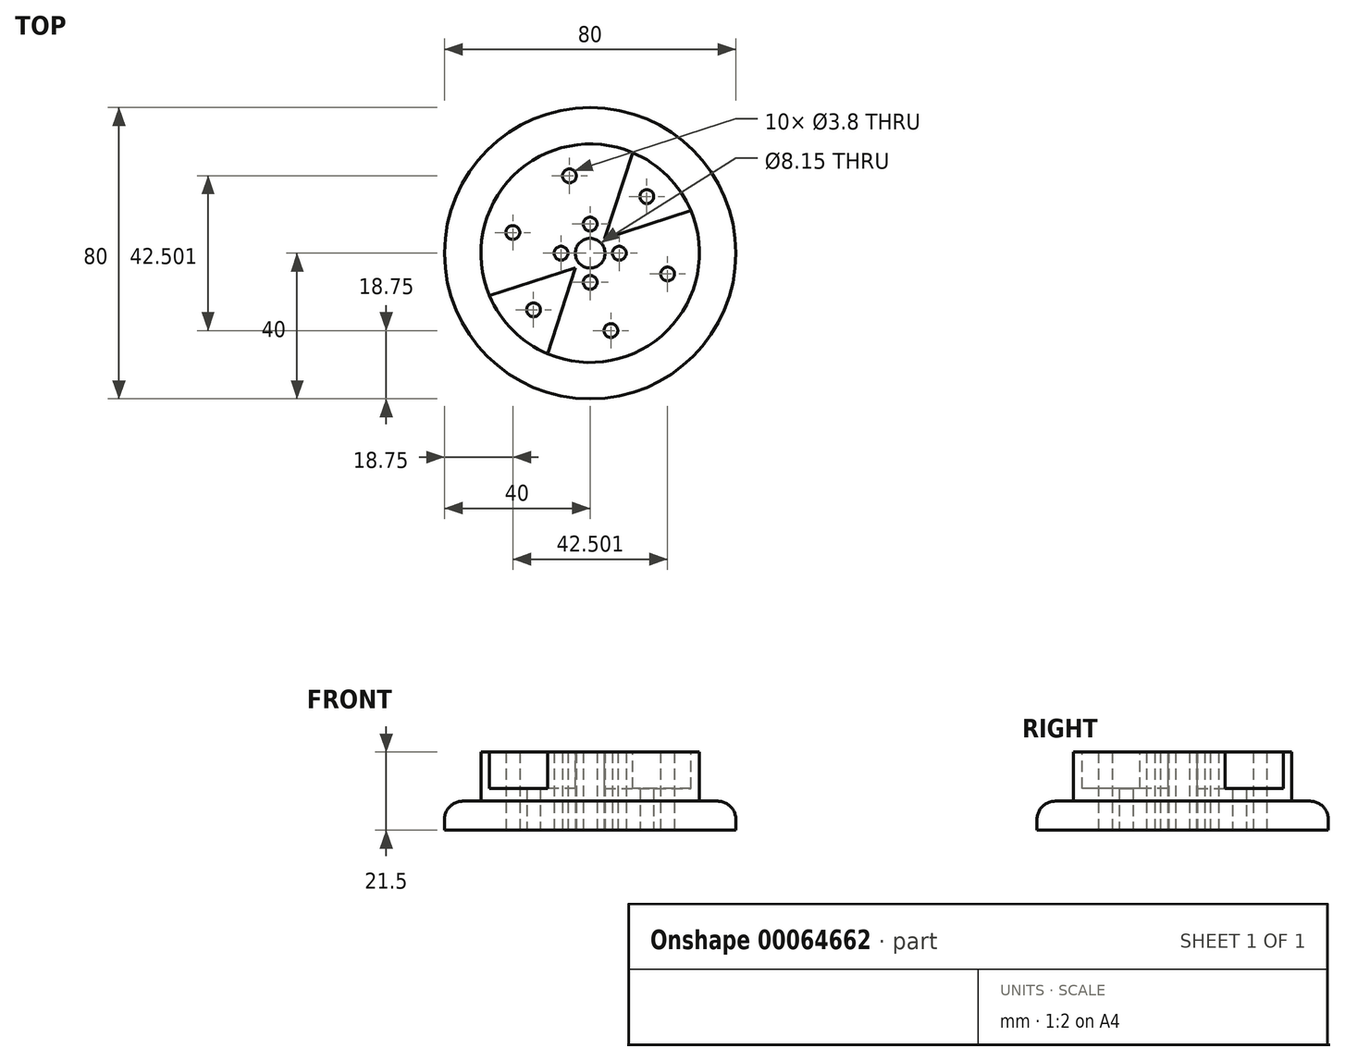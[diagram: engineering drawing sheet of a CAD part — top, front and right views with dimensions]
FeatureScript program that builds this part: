
annotation { "Feature Type Name" : "Feature", "Feature Type Description" : "" }
export const myFeature = defineFeature(function(context is Context, id is Id, definition is map)
    precondition{}
    {
        {
            var Q0;
            Q0=qCreatedBy(makeId("Top.planeOp"),FACE);
            var sketch = newSketch(context, id + "F0", { "sketchPlane" : qUnion([Q0])});
            skCircle(sketch, "E0", {"center": v(0, 0) * mm, "radius": 40 * mm});
            skCircle(sketch, "E1", {"center": v(0, 0) * mm, "radius": 4.08 * mm});
            skLineSegment(sketch, "E2", {"start": v(0, 0) * mm, "end": v(0, 8) * mm, "construction": true});
            skCircle(sketch, "E3", {"center": v(0, 8) * mm, "radius": 1.9 * mm});
            skCircle(sketch, "E4.1.0", {"center": v(-8, 0) * mm, "radius": 1.9 * mm});
            skCircle(sketch, "E4.2.0", {"center": v(0, -8) * mm, "radius": 1.9 * mm});
            skCircle(sketch, "E4.3.0", {"center": v(8, 0) * mm, "radius": 1.9 * mm});
            skCircle(sketch, "E5", {"center": v(0, 0) * mm, "radius": 30 * mm});
            skLineSegment(sketch, "E6", {"start": v(-8, 0) * mm, "end": v(0, -8) * mm, "construction": true});
            skLineSegment(sketch, "E7", {"start": v(8, 0) * mm, "end": v(0, -8) * mm, "construction": true});
            skLineSegment(sketch, "E8", {"start": v(0, 8) * mm, "end": v(8, 0) * mm, "construction": true});
            skLineSegment(sketch, "E9", {"start": v(-8, 0) * mm, "end": v(0, 8) * mm, "construction": true});
            skLineSegment(sketch, "E10", {"start": v(0, 0) * mm, "end": v(-15.56, -15.56) * mm, "construction": true});
            skCircle(sketch, "E11", {"center": v(-15.56, -15.56) * mm, "radius": 1.9 * mm});
            skCircle(sketch, "E12.1.0", {"center": v(5.7, -21.25) * mm, "radius": 1.9 * mm});
            skCircle(sketch, "E12.2.0", {"center": v(21.25, -5.7) * mm, "radius": 1.9 * mm});
            skCircle(sketch, "E12.3.0", {"center": v(15.56, 15.56) * mm, "radius": 1.9 * mm});
            skCircle(sketch, "E12.4.0", {"center": v(-5.7, 21.25) * mm, "radius": 1.9 * mm});
            skCircle(sketch, "E12.5.0", {"center": v(-21.25, 5.7) * mm, "radius": 1.9 * mm});
            skLineSegment(sketch, "E13", {"start": v(-4, 4) * mm, "end": v(4, -4) * mm, "construction": true});
            skSolve(sketch);
        }
        {
            var Q0;
            Q0=makeQuery(id+"F0.imprint","IMPRINT",FACE,{"disambiguationData":[TD([[makeQuery(id+"F0.imprint","IMPRINT",EDGE,{"derivedFrom":sQuery(id+"F0.wireOp",EDGE,"E1")}),-1.0]])]});
            extrude(context, id + "F1", {"entities" : qUnion([Q0]), "depth" : 21.5 * mm});
        }
        {
            var Q0;
            Q0 = qSketchRegion(id + "F0", true);
            extrude(context, id + "F2", {"entities" : qUnion([Q0]), "operationType" : NewBodyOperationType.ADD, "depth" : 8 * mm});
        }
        {
            var Q0;
            Q0=makeQuery(id+"F1.opExtrude","CAP_FACE",FACE,{"disambiguationData":[OSD([sQuery(id+"F0.wireOp",EDGE,"E1"),sQuery(id+"F0.wireOp",EDGE,"E3"),sQuery(id+"F0.wireOp",EDGE,"E4.1.0"),sQuery(id+"F0.wireOp",EDGE,"E4.2.0"),sQuery(id+"F0.wireOp",EDGE,"E4.3.0"),sQuery(id+"F0.wireOp",EDGE,"E5"),sQuery(id+"F0.wireOp",EDGE,"E11"),sQuery(id+"F0.wireOp",EDGE,"E12.1.0"),sQuery(id+"F0.wireOp",EDGE,"E12.2.0"),sQuery(id+"F0.wireOp",EDGE,"E12.3.0"),sQuery(id+"F0.wireOp",EDGE,"E12.4.0"),sQuery(id+"F0.wireOp",EDGE,"E12.5.0")])],"isStart":false});
            var sketch = newSketch(context, id + "F3", { "sketchPlane" : qUnion([Q0])});
            skLineSegment(sketch, "E14", {"start": v(0, 0) * mm, "end": v(-15.56, -15.56) * mm, "construction": true});
            skLineSegment(sketch, "E15", {"start": v(-8, 0) * mm, "end": v(0, -8) * mm, "construction": true});
            skLineSegment(sketch, "E16", {"start": v(0, -8) * mm, "end": v(8, 0) * mm, "construction": true});
            skLineSegment(sketch, "E17", {"start": v(8, 0) * mm, "end": v(0, 8) * mm, "construction": true});
            skLineSegment(sketch, "E18", {"start": v(0, 8) * mm, "end": v(-8, 0) * mm, "construction": true});
            skLineSegment(sketch, "E19", {"start": v(-4, 4) * mm, "end": v(4, -4) * mm, "construction": true});
            skLineSegment(sketch, "E20", {"start": v(-4, -4) * mm, "end": v(-27.63, -11.68) * mm});
            skLineSegment(sketch, "E21.MirrorCS", {"start": v(-4, -4) * mm, "end": v(-11.68, -27.63) * mm});
            skLineSegment(sketch, "E22.MirrorCS", {"start": v(4, 4) * mm, "end": v(11.68, 27.63) * mm});
            skLineSegment(sketch, "E23.MirrorCS", {"start": v(4, 4) * mm, "end": v(27.63, 11.68) * mm});
            skSolve(sketch);
        }
        {
            var Q0;
            Q0 = qSketchRegion(id + "F3", true);
            var Q1;
            {var subQ0=sQuery(id+"F3.wireOp",EDGE,"E20");Q1=makeQuery(id+"F3.imprint","IMPRINT",FACE,{"disambiguationData":[TD([[makeQuery(id+"F3.imprint","IMPRINT",EDGE,{"derivedFrom":subQ0}),1.0]])]});}
            var Q2;
            {var subQ0=sQuery(id+"F3.wireOp",EDGE,"E22.MirrorCS");Q2=makeQuery(id+"F3.imprint","IMPRINT",FACE,{"disambiguationData":[TD([[makeQuery(id+"F3.imprint","IMPRINT",EDGE,{"derivedFrom":subQ0}),-1.0]])]});}
            extrude(context, id + "F4", {"entities" : qUnion([Q0, Q1, Q2]), "operationType" : NewBodyOperationType.REMOVE, "oppositeDirection" : true, "depth" : 10 * mm});
        }
        {
            var Q0;
            Q0=makeQuery(id+"F2.opExtrude","CAP_EDGE",EDGE,{"disambiguationData":[OSD([sQuery(id+"F0.wireOp",EDGE,"E0")])],"isStart":false});
            fillet(context, id + "F5", {"entities" : qUnion([Q0]), "radius" : 5 * mm, "tangentPropagation" : true, "allowEdgeOverflow" : false});
        }
    });
